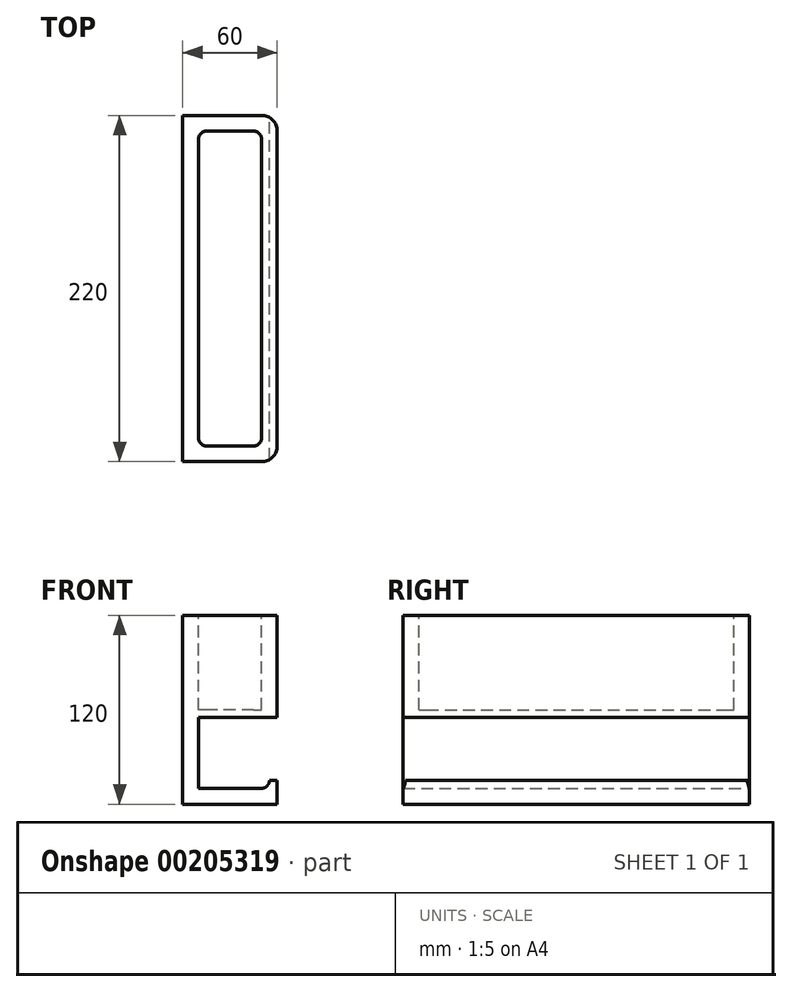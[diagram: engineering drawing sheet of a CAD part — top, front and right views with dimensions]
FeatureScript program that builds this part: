
annotation { "Feature Type Name" : "Feature", "Feature Type Description" : "" }
export const myFeature = defineFeature(function(context is Context, id is Id, definition is map)
    precondition{}
    {
        {
            var Q0;
            Q0=qCreatedBy(makeId("Front.planeOp"),FACE);
            var sketch = newSketch(context, id + "F0", { "sketchPlane" : qUnion([Q0])});
            skLineSegment(sketch, "E0.bottom", {"start": v(30, -60) * mm, "end": v(-30, -60) * mm});
            skLineSegment(sketch, "E0.top", {"start": v(30, 60) * mm, "end": v(-30, 60) * mm});
            skLineSegment(sketch, "E0.left", {"start": v(30, -60) * mm, "end": v(30, 60) * mm});
            skLineSegment(sketch, "E0.right", {"start": v(-30, -60) * mm, "end": v(-30, 60) * mm});
            skPoint(sketch, "E0.middle", {"position": v(0, 0) * mm});
            skLineSegment(sketch, "E1.bottom", {"start": v(25, -50) * mm, "end": v(-20, -50) * mm});
            skLineSegment(sketch, "E1.top", {"start": v(30, -5) * mm, "end": v(-20, -5) * mm});
            skLineSegment(sketch, "E1.left", {"start": v(30, -50) * mm, "end": v(30, -5) * mm});
            skLineSegment(sketch, "E1.right", {"start": v(-20, -50) * mm, "end": v(-20, -5) * mm});
            skLineSegment(sketch, "E2.top", {"start": v(30, -45) * mm, "end": v(25, -45) * mm});
            skLineSegment(sketch, "E2.left", {"start": v(30, -50) * mm, "end": v(30, -45) * mm});
            skLineSegment(sketch, "E2.right", {"start": v(25, -50) * mm, "end": v(25, -45) * mm});
            skSolve(sketch);
        }
        {
            var Q0;
            {var subQ2=sQuery(id+"F0.wireOp",EDGE,"E0.bottom");Q0=makeQuery(id+"F0.imprint","IMPRINT",FACE,{"disambiguationData":[TD([[makeQuery(id+"F0.imprint","IMPRINT",EDGE,{"derivedFrom":subQ2}),-1.0]])]});}
            extrude(context, id + "F1", {"entities" : qUnion([Q0]), "endBound" : BoundingType.SYMMETRIC, "depth" : 220 * mm, "offsetDistance" : 25 * mm});
        }
        {
            var Q0;
            Q0=makeQuery(id+"F1.opExtrude","SWEPT_FACE",FACE,{"disambiguationData":[OSD([sQuery(id+"F0.wireOp",EDGE,"E0.top")])]});
            var sketch = newSketch(context, id + "F2", { "sketchPlane" : qUnion([Q0])});
            skLineSegment(sketch, "E3.0", {"start": v(20, 100) * mm, "end": v(-20, 100) * mm});
            skLineSegment(sketch, "E3.1", {"start": v(20, -100) * mm, "end": v(20, 100) * mm});
            skLineSegment(sketch, "E3.2", {"start": v(-20, -100) * mm, "end": v(20, -100) * mm});
            skLineSegment(sketch, "E3.3", {"start": v(-20, 100) * mm, "end": v(-20, -100) * mm});
            skSolve(sketch);
        }
        {
            var Q0;
            Q0=makeQuery(id+"F2.imprint","IMPRINT",FACE,{"disambiguationData":[TD([[makeQuery(id+"F2.imprint","IMPRINT",EDGE,{"derivedFrom":sQuery(id+"F2.wireOp",EDGE,"E3.0")}),1.0]])]});
            extrude(context, id + "F3", {"entities" : qUnion([Q0]), "operationType" : NewBodyOperationType.REMOVE, "oppositeDirection" : true, "depth" : 60 * mm, "offsetDistance" : 25 * mm});
        }
        {
            var Q0;
            Q0=makeQuery(id+"F3.boolean.opBoolean","COPY",EDGE,{"derivedFrom":makeQuery(id+"F3.opExtrude","SWEPT_EDGE",EDGE,{"disambiguationData":[OSD([sQuery(id+"F2.wireOp",EDGE,"E3.0"),sQuery(id+"F2.wireOp",EDGE,"E3.3")])]})});
            var Q1;
            Q1=makeQuery(id+"F3.boolean.opBoolean","COPY",EDGE,{"derivedFrom":makeQuery(id+"F3.opExtrude","SWEPT_EDGE",EDGE,{"disambiguationData":[OSD([sQuery(id+"F2.wireOp",EDGE,"E3.0"),sQuery(id+"F2.wireOp",EDGE,"E3.1")])]})});
            var Q2;
            Q2=makeQuery(id+"F3.boolean.opBoolean","COPY",EDGE,{"derivedFrom":makeQuery(id+"F3.opExtrude","SWEPT_EDGE",EDGE,{"disambiguationData":[OSD([sQuery(id+"F2.wireOp",EDGE,"E3.2"),sQuery(id+"F2.wireOp",EDGE,"E3.3")])]})});
            var Q3;
            Q3=makeQuery(id+"F3.boolean.opBoolean","COPY",EDGE,{"derivedFrom":makeQuery(id+"F3.opExtrude","SWEPT_EDGE",EDGE,{"disambiguationData":[OSD([sQuery(id+"F2.wireOp",EDGE,"E3.1"),sQuery(id+"F2.wireOp",EDGE,"E3.2")])]})});
            var Q4;
            Q4=makeQuery(id+"F1.opExtrude","SWEPT_EDGE",EDGE,{"disambiguationData":[OSD([sQuery(id+"F0.wireOp",EDGE,"E1.bottom"),sQuery(id+"F0.wireOp",EDGE,"E2.right")])]});
            fillet(context, id + "F4", {"entities" : qUnion([Q0, Q1, Q2, Q3, Q4]), "radius" : 5 * mm, "tangentPropagation" : true, "allowEdgeOverflow" : false});
        }
        {
            var Q0;
            Q0=makeQuery(id+"F1.opExtrude","CAP_EDGE",EDGE,{"disambiguationData":[OSD([sQuery(id+"F0.wireOp",EDGE,"E0.left")])],"isStart":false});
            var Q1;
            Q1=makeQuery(id+"F1.opExtrude","CAP_EDGE",EDGE,{"disambiguationData":[OSD([sQuery(id+"F0.wireOp",EDGE,"E0.left")])],"isStart":true});
            fillet(context, id + "F5", {"entities" : qUnion([Q0, Q1]), "radius" : 10 * mm, "tangentPropagation" : true, "allowEdgeOverflow" : false});
        }
    });
